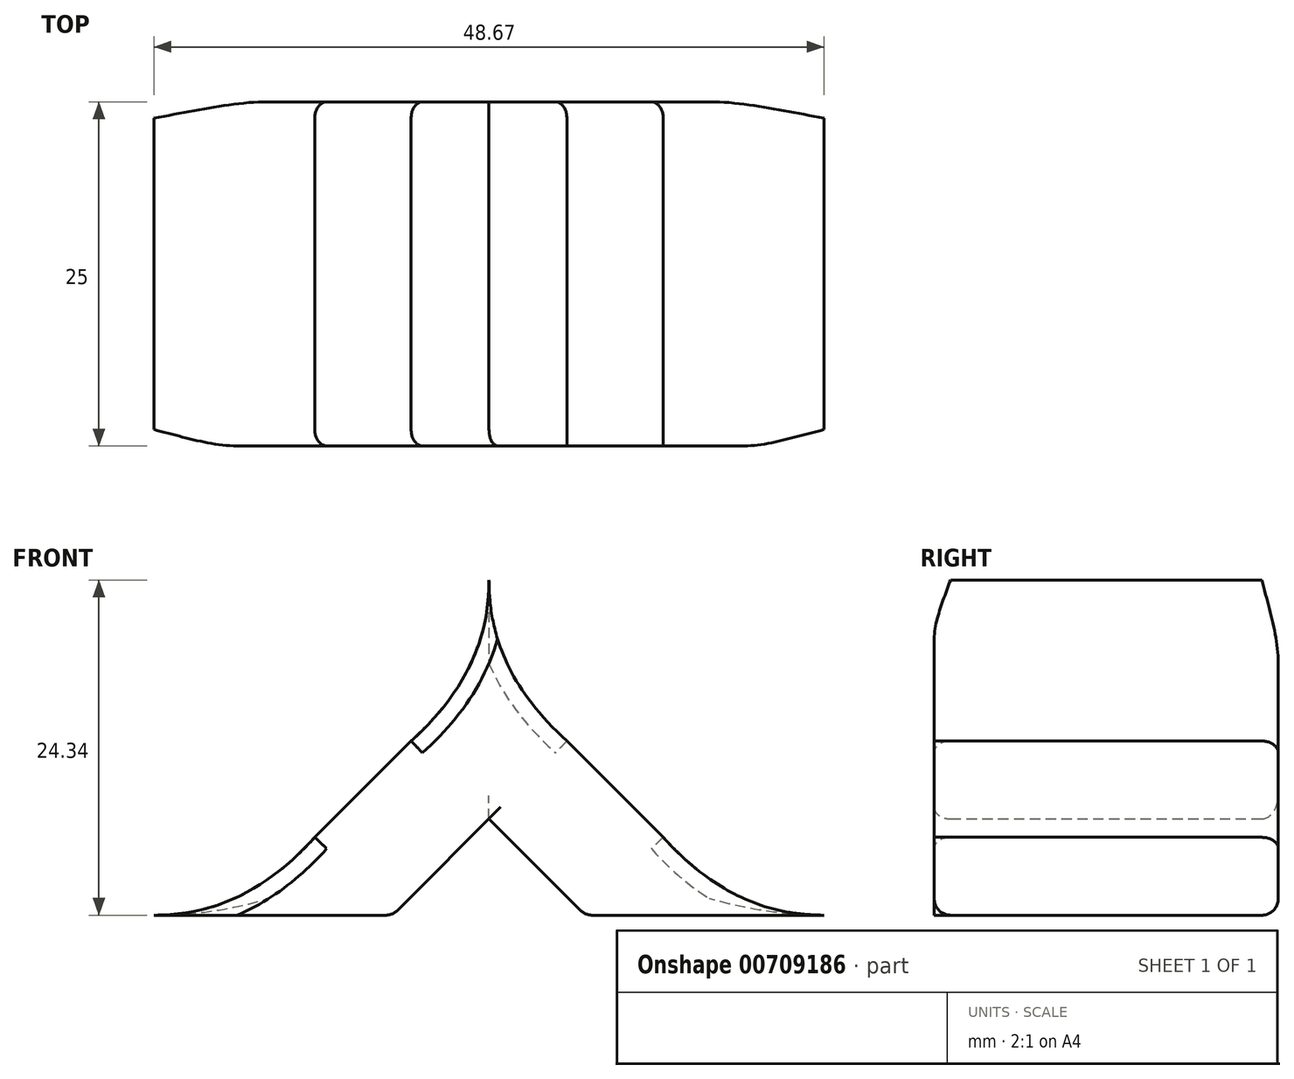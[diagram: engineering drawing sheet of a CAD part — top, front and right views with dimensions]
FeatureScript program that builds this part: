
annotation { "Feature Type Name" : "Feature", "Feature Type Description" : "" }
export const myFeature = defineFeature(function(context is Context, id is Id, definition is map)
    precondition{}
    {
        {
            var Q0;
            Q0=qCreatedBy(makeId("Front.planeOp"),FACE);
            var sketch = newSketch(context, id + "F0", { "sketchPlane" : qUnion([Q0])});
            skLineSegment(sketch, "E0.bottom", {"start": v(-9.08, 0) * mm, "end": v(8.92, 0) * mm});
            skLineSegment(sketch, "E1", {"start": v(-16.08, 7) * mm, "end": v(-9.08, 0) * mm});
            skFitSpline(sketch, "E2", {"points": [v(-3.42, 5.66) * mm, v(8.92, 0) * mm], "startDerivative": vector(15.8, -17.57) * mm, "endDerivative": vector(6.16, 0) * mm});
            skFitSpline(sketch, "E3.MirrorCS", {"points": [v(-10.42, 12.66) * mm, v(-16.08, 25) * mm], "startDerivative": vector(-17.57, 15.8) * mm, "endDerivative": vector(0, 6.16) * mm});
            skPoint(sketch, "E4.end.orphan", {"position": v(-12.58, 3.5) * mm});
            skLineSegment(sketch, "E5", {"start": v(-10.42, 12.66) * mm, "end": v(-3.42, 5.66) * mm});
            skFitSpline(sketch, "E6.MirrorCS", {"points": [v(-28.73, 5.66) * mm, v(-41.08, 0) * mm], "startDerivative": vector(-15.8, -17.57) * mm, "endDerivative": vector(-6.16, 0) * mm});
            skLineSegment(sketch, "E7.MirrorCS", {"start": v(-23.08, 0) * mm, "end": v(-41.08, 0) * mm});
            skLineSegment(sketch, "E8.MirrorCS", {"start": v(-21.73, 12.66) * mm, "end": v(-28.73, 5.66) * mm});
            skFitSpline(sketch, "E9.MirrorCS", {"points": [v(-21.73, 12.66) * mm, v(-16.08, 25) * mm], "startDerivative": vector(17.57, 15.8) * mm, "endDerivative": vector(0, 6.16) * mm});
            skPoint(sketch, "E10.MirrorP", {"position": v(-19.58, 3.5) * mm});
            skLineSegment(sketch, "E11.MirrorCS", {"start": v(-16.08, 7) * mm, "end": v(-23.08, 0) * mm});
            skSolve(sketch);
        }
        {
            var Q0;
            {var subQ0=sQuery(id+"F0.wireOp",EDGE,"E1");Q0=makeQuery(id+"F0.imprint","IMPRINT",FACE,{"disambiguationData":[TD([[makeQuery(id+"F0.imprint","IMPRINT",EDGE,{"derivedFrom":subQ0}),1.0]])]});}
            extrude(context, id + "F1", {"entities" : qUnion([Q0]), "depth" : 25 * mm, "offsetDistance" : 25 * mm});
        }
        {
            var Q0;
            Q0=makeQuery(id+"F1.opExtrude","CAP_EDGE",EDGE,{"disambiguationData":[OSD([sQuery(id+"F0.wireOp",EDGE,"E0.left")])],"isStart":false});
            var Q1;
            Q1=makeQuery(id+"F1.opExtrude","CAP_EDGE",EDGE,{"disambiguationData":[OSD([sQuery(id+"F0.wireOp",EDGE,"E1")])],"isStart":false});
            var Q2;
            Q2=makeQuery(id+"F1.opExtrude","CAP_EDGE",EDGE,{"disambiguationData":[OSD([sQuery(id+"F0.wireOp",EDGE,"E0.bottom")])],"isStart":false});
            var Q3;
            Q3=makeQuery(id+"F1.opExtrude","CAP_EDGE",EDGE,{"disambiguationData":[OSD([sQuery(id+"F0.wireOp",EDGE,"E0.left")])],"isStart":true});
            var Q4;
            Q4=makeQuery(id+"F1.opExtrude","CAP_EDGE",EDGE,{"disambiguationData":[OSD([sQuery(id+"F0.wireOp",EDGE,"E1")])],"isStart":true});
            var Q5;
            Q5=makeQuery(id+"F1.opExtrude","CAP_EDGE",EDGE,{"disambiguationData":[OSD([sQuery(id+"F0.wireOp",EDGE,"E0.bottom")])],"isStart":true});
            var Q6;
            Q6=makeQuery(id+"F1.opExtrude","CAP_EDGE",EDGE,{"disambiguationData":[OSD([sQuery(id+"F0.wireOp",EDGE,"E5")])],"isStart":true});
            var Q7;
            Q7=makeQuery(id+"F1.opExtrude","CAP_EDGE",EDGE,{"disambiguationData":[OSD([sQuery(id+"F0.wireOp",EDGE,"E3.MirrorCS")])],"isStart":true});
            var Q8;
            Q8=makeQuery(id+"F1.opExtrude","CAP_EDGE",EDGE,{"disambiguationData":[OSD([sQuery(id+"F0.wireOp",EDGE,"E2")])],"isStart":true});
            var Q9;
            Q9=makeQuery(id+"F1.opExtrude","CAP_EDGE",EDGE,{"disambiguationData":[OSD([sQuery(id+"F0.wireOp",EDGE,"E11.MirrorCS")])],"isStart":true});
            var Q10;
            Q10=makeQuery(id+"F1.opExtrude","CAP_EDGE",EDGE,{"disambiguationData":[OSD([sQuery(id+"F0.wireOp",EDGE,"E7.MirrorCS")])],"isStart":true});
            var Q11;
            Q11=makeQuery(id+"F1.opExtrude","CAP_EDGE",EDGE,{"disambiguationData":[OSD([sQuery(id+"F0.wireOp",EDGE,"E8.MirrorCS")])],"isStart":true});
            var Q12;
            Q12=makeQuery(id+"F1.opExtrude","CAP_EDGE",EDGE,{"disambiguationData":[OSD([sQuery(id+"F0.wireOp",EDGE,"E9.MirrorCS")])],"isStart":true});
            var Q13;
            Q13=makeQuery(id+"F1.opExtrude","CAP_EDGE",EDGE,{"disambiguationData":[OSD([sQuery(id+"F0.wireOp",EDGE,"E6.MirrorCS")])],"isStart":true});
            var Q14;
            Q14=makeQuery(id+"F1.opExtrude","CAP_EDGE",EDGE,{"disambiguationData":[OSD([sQuery(id+"F0.wireOp",EDGE,"E8.MirrorCS")])],"isStart":false});
            var Q15;
            Q15=makeQuery(id+"F1.opExtrude","CAP_EDGE",EDGE,{"disambiguationData":[OSD([sQuery(id+"F0.wireOp",EDGE,"E9.MirrorCS")])],"isStart":false});
            var Q16;
            Q16=makeQuery(id+"F1.opExtrude","CAP_EDGE",EDGE,{"disambiguationData":[OSD([sQuery(id+"F0.wireOp",EDGE,"E6.MirrorCS")])],"isStart":false});
            var Q17;
            Q17=makeQuery(id+"F1.opExtrude","SWEPT_EDGE",EDGE,{"disambiguationData":[OSD([sQuery(id+"F0.wireOp",EDGE,"E7.MirrorCS"),sQuery(id+"F0.wireOp",EDGE,"E11.MirrorCS")])]});
            var Q18;
            Q18=makeQuery(id+"F1.opExtrude","SWEPT_EDGE",EDGE,{"disambiguationData":[OSD([sQuery(id+"F0.wireOp",EDGE,"E0.bottom"),sQuery(id+"F0.wireOp",EDGE,"E1")])]});
            fillet(context, id + "F2", {"entities" : qUnion([Q0, Q1, Q2, Q3, Q4, Q5, Q6, Q7, Q8, Q9, Q10, Q11, Q12, Q13, Q14, Q15, Q16, Q17, Q18]), "radius" : 1.2 * mm, "tangentPropagation" : true, "allowEdgeOverflow" : false});
        }
    });
